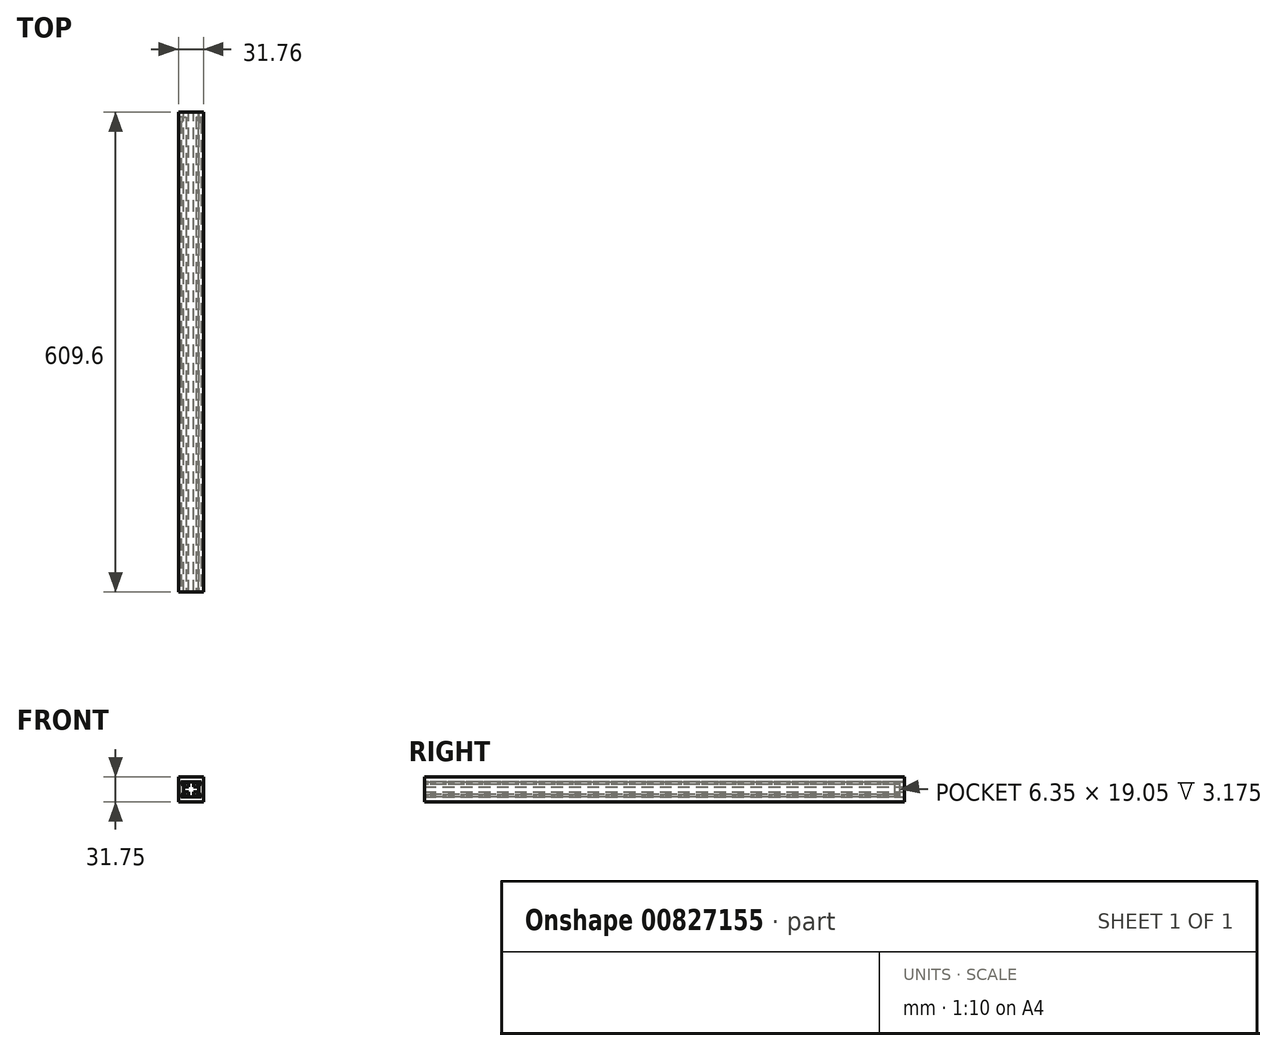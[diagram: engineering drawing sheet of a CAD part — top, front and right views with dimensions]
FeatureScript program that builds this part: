
annotation { "Feature Type Name" : "Feature", "Feature Type Description" : "" }
export const myFeature = defineFeature(function(context is Context, id is Id, definition is map)
    precondition{}
    {
        {
            var Q0;
            Q0=qCreatedBy(makeId("Top.planeOp"),FACE);
            var sketch = newSketch(context, id + "F0", { "sketchPlane" : qUnion([Q0])});
            skLineSegment(sketch, "E0", {"start": v(0, 0) * mm, "end": v(3.17, 0) * mm});
            skLineSegment(sketch, "E1", {"start": v(3.17, 0) * mm, "end": v(-3.17, 0) * mm});
            skLineSegment(sketch, "E2.bottom", {"start": v(3.17, 0) * mm, "end": v(9.53, 0) * mm});
            skLineSegment(sketch, "E2.top", {"start": v(3.18, 609.6) * mm, "end": v(9.53, 609.6) * mm});
            skLineSegment(sketch, "E2.left", {"start": v(3.18, 0) * mm, "end": v(3.18, 609.6) * mm});
            skLineSegment(sketch, "E2.right", {"start": v(9.53, 0) * mm, "end": v(9.53, 609.6) * mm});
            skLineSegment(sketch, "E3.bottom", {"start": v(-3.17, 0) * mm, "end": v(-9.53, 0) * mm});
            skLineSegment(sketch, "E3.top", {"start": v(-3.18, 609.6) * mm, "end": v(-9.53, 609.6) * mm});
            skLineSegment(sketch, "E3.left", {"start": v(-3.17, 0) * mm, "end": v(-3.18, 609.6) * mm});
            skLineSegment(sketch, "E3.right", {"start": v(-9.53, 0) * mm, "end": v(-9.53, 609.6) * mm});
            skPoint(sketch, "E4", {"position": v(0, 0) * mm});
            skSolve(sketch);
        }
        {
            var Q0;
            Q0=makeQuery(id+"F0.imprint","IMPRINT",FACE,{"disambiguationData":[TD([[makeQuery(id+"F0.imprint","IMPRINT",EDGE,{"derivedFrom":sQuery(id+"F0.wireOp",EDGE,"E3.bottom")}),-1.0]])]});
            var Q1;
            Q1=makeQuery(id+"F0.imprint","IMPRINT",FACE,{"disambiguationData":[TD([[makeQuery(id+"F0.imprint","IMPRINT",EDGE,{"derivedFrom":sQuery(id+"F0.wireOp",EDGE,"E2.bottom")}),1.0]])]});
            extrude(context, id + "F1", {"entities" : qUnion([Q0, Q1]), "depth" : 6.35 * mm, "offsetDistance" : 25.4 * mm});
        }
        {
            var Q0;
            Q0=qSketchRegion(id+"F0",true);
            extrude(context, id + "F2", {"entities" : qUnion([Q0]), "oppositeDirection" : true, "depth" : 12.7 * mm, "offsetDistance" : 25.4 * mm});
        }
        {
            var Q0;
            Q0=qSketchRegion(id+"F0",true);
            extrude(context, id + "F3", {"entities" : qUnion([Q0]), "operationType" : NewBodyOperationType.REMOVE, "oppositeDirection" : true, "depth" : 6.35 * mm, "offsetDistance" : 25.4 * mm});
        }
        {
            var Q0;
            Q0=qCreatedBy(makeId("Front.planeOp"),FACE);
            var sketch = newSketch(context, id + "F4", { "sketchPlane" : qUnion([Q0])});
            skPoint(sketch, "E5", {"position": v(-9.53, 6.35) * mm});
            skPoint(sketch, "E6", {"position": v(9.53, 6.35) * mm});
            skPoint(sketch, "E7", {"position": v(9.53, -12.7) * mm});
            skPoint(sketch, "E8", {"position": v(-9.53, -12.7) * mm});
            skLineSegment(sketch, "E9", {"start": v(-9.53, 6.35) * mm, "end": v(9.53, 6.35) * mm});
            skLineSegment(sketch, "E10", {"start": v(-9.53, -12.7) * mm, "end": v(9.53, -12.7) * mm});
            skLineSegment(sketch, "E11", {"start": v(9.53, 6.35) * mm, "end": v(9.53, -12.7) * mm});
            skLineSegment(sketch, "E12", {"start": v(-9.53, 6.35) * mm, "end": v(-9.53, -12.7) * mm});
            skLineSegment(sketch, "E13.left", {"start": v(-15.88, 12.7) * mm, "end": v(-15.88, -19.05) * mm});
            skLineSegment(sketch, "E14", {"start": v(-15.88, 12.7) * mm, "end": v(15.88, 12.7) * mm});
            skLineSegment(sketch, "E15", {"start": v(-15.88, -19.05) * mm, "end": v(15.88, -19.05) * mm});
            skLineSegment(sketch, "E16", {"start": v(15.88, -19.05) * mm, "end": v(15.88, 12.7) * mm});
            skSolve(sketch);
        }
        {
            var Q0;
            Q0=makeQuery(id+"F4.imprint","IMPRINT",FACE,{"disambiguationData":[TD([[makeQuery(id+"F4.imprint","IMPRINT",EDGE,{"derivedFrom":sQuery(id+"F4.wireOp",EDGE,"E9")}),1.0]])]});
            extrude(context, id + "F5", {"entities" : qUnion([Q0]), "oppositeDirection" : true, "depth" : 609.6 * mm, "offsetDistance" : 25.4 * mm});
        }
        {
            var Q0;
            Q0=makeQuery(id+"F5.opExtrude","CAP_FACE",FACE,{"disambiguationData":[OSD([sQuery(id+"F4.wireOp",EDGE,"E9"),sQuery(id+"F4.wireOp",EDGE,"E10"),sQuery(id+"F4.wireOp",EDGE,"E11"),sQuery(id+"F4.wireOp",EDGE,"E12"),sQuery(id+"F4.wireOp",EDGE,"E13.left"),sQuery(id+"F4.wireOp",EDGE,"E14"),sQuery(id+"F4.wireOp",EDGE,"E15"),sQuery(id+"F4.wireOp",EDGE,"E16")])],"isStart":true});
            var sketch = newSketch(context, id + "F6", { "sketchPlane" : qUnion([Q0])});
            skPoint(sketch, "E17", {"position": v(6.35, -9.53) * mm});
            skPoint(sketch, "E18", {"position": v(12.7, -12.7) * mm});
            skLineSegment(sketch, "E19.bottom", {"start": v(6.35, -9.53) * mm, "end": v(12.7, -9.53) * mm});
            skLineSegment(sketch, "E19.top", {"start": v(6.35, -12.7) * mm, "end": v(12.7, -12.7) * mm});
            skLineSegment(sketch, "E19.left", {"start": v(6.35, -9.53) * mm, "end": v(6.35, -12.7) * mm});
            skLineSegment(sketch, "E19.right", {"start": v(12.7, -9.53) * mm, "end": v(12.7, -12.7) * mm});
            skPoint(sketch, "E20", {"position": v(-6.35, 3.18) * mm});
            skPoint(sketch, "E21", {"position": v(6.35, 3.17) * mm});
            skPoint(sketch, "E22", {"position": v(-6.35, -9.53) * mm});
            skLineSegment(sketch, "E23.bottom", {"start": v(6.35, 3.17) * mm, "end": v(12.7, 3.17) * mm});
            skLineSegment(sketch, "E23.top", {"start": v(6.35, 6.35) * mm, "end": v(12.7, 6.35) * mm});
            skLineSegment(sketch, "E23.left", {"start": v(6.35, 3.17) * mm, "end": v(6.35, 6.35) * mm});
            skLineSegment(sketch, "E23.right", {"start": v(12.7, 3.17) * mm, "end": v(12.7, 6.35) * mm});
            skLineSegment(sketch, "E24.bottom", {"start": v(-12.7, -9.53) * mm, "end": v(-6.35, -9.53) * mm});
            skLineSegment(sketch, "E24.top", {"start": v(-12.7, -12.7) * mm, "end": v(-6.35, -12.7) * mm});
            skLineSegment(sketch, "E24.left", {"start": v(-12.7, -9.53) * mm, "end": v(-12.7, -12.7) * mm});
            skLineSegment(sketch, "E24.right", {"start": v(-6.35, -9.53) * mm, "end": v(-6.35, -12.7) * mm});
            skLineSegment(sketch, "E25.bottom", {"start": v(-6.35, 3.18) * mm, "end": v(-12.7, 3.18) * mm});
            skLineSegment(sketch, "E25.top", {"start": v(-6.35, 6.35) * mm, "end": v(-12.7, 6.35) * mm});
            skLineSegment(sketch, "E25.left", {"start": v(-6.35, 3.18) * mm, "end": v(-6.35, 6.35) * mm});
            skLineSegment(sketch, "E25.right", {"start": v(-12.7, 3.17) * mm, "end": v(-12.7, 6.35) * mm});
            skSolve(sketch);
        }
        {
            var Q0;
            {var subQ0=sQuery(id+"F6.wireOp",EDGE,"E25.right");Q0=makeQuery(id+"F6.imprint","IMPRINT",FACE,{"disambiguationData":[TD([[makeQuery(id+"F6.imprint","IMPRINT",EDGE,{"derivedFrom":subQ0}),-1.0]])]});}
            var Q1;
            {var subQ0=sQuery(id+"F6.wireOp",EDGE,"E25.left");Q1=makeQuery(id+"F6.imprint","IMPRINT",FACE,{"disambiguationData":[TD([[makeQuery(id+"F6.imprint","IMPRINT",EDGE,{"derivedFrom":subQ0}),1.0]])]});}
            var Q2;
            {var subQ0=sQuery(id+"F6.wireOp",EDGE,"E23.left");Q2=makeQuery(id+"F6.imprint","IMPRINT",FACE,{"disambiguationData":[TD([[makeQuery(id+"F6.imprint","IMPRINT",EDGE,{"derivedFrom":subQ0}),-1.0]])]});}
            var Q3;
            {var subQ0=sQuery(id+"F6.wireOp",EDGE,"E23.right");Q3=makeQuery(id+"F6.imprint","IMPRINT",FACE,{"disambiguationData":[TD([[makeQuery(id+"F6.imprint","IMPRINT",EDGE,{"derivedFrom":subQ0}),1.0]])]});}
            var Q4;
            {var subQ0=sQuery(id+"F6.wireOp",EDGE,"E24.left");Q4=makeQuery(id+"F6.imprint","IMPRINT",FACE,{"disambiguationData":[TD([[makeQuery(id+"F6.imprint","IMPRINT",EDGE,{"derivedFrom":subQ0}),1.0]])]});}
            var Q5;
            {var subQ0=sQuery(id+"F6.wireOp",EDGE,"E24.right");Q5=makeQuery(id+"F6.imprint","IMPRINT",FACE,{"disambiguationData":[TD([[makeQuery(id+"F6.imprint","IMPRINT",EDGE,{"derivedFrom":subQ0}),-1.0]])]});}
            var Q6;
            {var subQ0=sQuery(id+"F6.wireOp",EDGE,"E19.left");Q6=makeQuery(id+"F6.imprint","IMPRINT",FACE,{"disambiguationData":[TD([[makeQuery(id+"F6.imprint","IMPRINT",EDGE,{"derivedFrom":subQ0}),1.0]])]});}
            var Q7;
            {var subQ0=sQuery(id+"F6.wireOp",EDGE,"E19.right");Q7=makeQuery(id+"F6.imprint","IMPRINT",FACE,{"disambiguationData":[TD([[makeQuery(id+"F6.imprint","IMPRINT",EDGE,{"derivedFrom":subQ0}),-1.0]])]});}
            extrude(context, id + "F7", {"entities" : qUnion([Q0, Q1, Q2, Q3, Q4, Q5, Q6, Q7]), "operationType" : NewBodyOperationType.REMOVE, "oppositeDirection" : true, "depth" : 603.25 * mm, "offsetDistance" : 25.4 * mm});
        }
        {
            var Q0;
            Q0=makeQuery(id+"F5.opExtrude","CAP_FACE",FACE,{"disambiguationData":[OSD([sQuery(id+"F4.wireOp",EDGE,"E9"),sQuery(id+"F4.wireOp",EDGE,"E10"),sQuery(id+"F4.wireOp",EDGE,"E11"),sQuery(id+"F4.wireOp",EDGE,"E12"),sQuery(id+"F4.wireOp",EDGE,"E13.left"),sQuery(id+"F4.wireOp",EDGE,"E14"),sQuery(id+"F4.wireOp",EDGE,"E15"),sQuery(id+"F4.wireOp",EDGE,"E16")])],"isStart":false});
            var sketch = newSketch(context, id + "F8", { "sketchPlane" : qUnion([Q0])});
            skLineSegment(sketch, "E26.right", {"start": v(-13.97, 6.35) * mm, "end": v(-13.97, -12.7) * mm});
            skLineSegment(sketch, "E27.bottom", {"start": v(-13.97, 6.35) * mm, "end": v(-10.8, 6.35) * mm});
            skLineSegment(sketch, "E27.top", {"start": v(-13.97, -12.7) * mm, "end": v(-10.8, -12.7) * mm});
            skLineSegment(sketch, "E27.right", {"start": v(-10.8, 6.35) * mm, "end": v(-10.8, -12.7) * mm});
            skLineSegment(sketch, "E28.bottom", {"start": v(10.8, 6.35) * mm, "end": v(13.97, 6.35) * mm});
            skLineSegment(sketch, "E28.top", {"start": v(10.8, -12.7) * mm, "end": v(13.97, -12.7) * mm});
            skLineSegment(sketch, "E28.left", {"start": v(10.8, 6.35) * mm, "end": v(10.8, -12.7) * mm});
            skLineSegment(sketch, "E28.right", {"start": v(13.97, 6.35) * mm, "end": v(13.97, -12.7) * mm});
            skSolve(sketch);
        }
        {
            var Q0;
            {var subQ1=makeQuery(id+"F7.boolean.opBoolean","COPY",EDGE,{"derivedFrom":makeQuery(id+"F7.opExtrude","CAP_EDGE",EDGE,{"disambiguationData":[OSD([sQuery(id+"F6.wireOp",EDGE,"E23.right")])],"isStart":false})});Q0=makeQuery(id+"F8.imprint","IMPRINT",FACE,{"disambiguationData":[TD([[makeQuery(id+"F8.imprint","IMPRINT",EDGE,{"derivedFrom":subQ1}),-1.0]])]});}
            var Q1;
            {var subQ2=sQuery(id+"F8.wireOp",EDGE,"E26.right");Q1=makeQuery(id+"F8.imprint","IMPRINT",FACE,{"disambiguationData":[TD([[makeQuery(id+"F8.imprint","IMPRINT",EDGE,{"derivedFrom":subQ2}),1.0]])]});}
            var Q2;
            {var subQ1=makeQuery(id+"F7.boolean.opBoolean","COPY",EDGE,{"derivedFrom":makeQuery(id+"F7.opExtrude","CAP_EDGE",EDGE,{"disambiguationData":[OSD([sQuery(id+"F6.wireOp",EDGE,"E19.right")])],"isStart":false})});Q2=makeQuery(id+"F8.imprint","IMPRINT",FACE,{"disambiguationData":[TD([[makeQuery(id+"F8.imprint","IMPRINT",EDGE,{"derivedFrom":subQ1}),1.0]])]});}
            extrude(context, id + "F9", {"entities" : qUnion([Q0, Q1, Q2]), "operationType" : NewBodyOperationType.REMOVE, "oppositeDirection" : true, "depth" : 12.7 * mm, "offsetDistance" : 25.4 * mm});
        }
        {
            var Q0;
            {var subQ2=sQuery(id+"F8.wireOp",EDGE,"E26.right");Q0=makeQuery(id+"F8.imprint","IMPRINT",FACE,{"disambiguationData":[TD([[makeQuery(id+"F8.imprint","IMPRINT",EDGE,{"derivedFrom":subQ2}),1.0]])]});}
            var Q1;
            {var subQ1=makeQuery(id+"F7.boolean.opBoolean","COPY",EDGE,{"derivedFrom":makeQuery(id+"F7.opExtrude","CAP_EDGE",EDGE,{"disambiguationData":[OSD([sQuery(id+"F6.wireOp",EDGE,"E23.right")])],"isStart":false})});Q1=makeQuery(id+"F8.imprint","IMPRINT",FACE,{"disambiguationData":[TD([[makeQuery(id+"F8.imprint","IMPRINT",EDGE,{"derivedFrom":subQ1}),-1.0]])]});}
            var Q2;
            {var subQ1=makeQuery(id+"F7.boolean.opBoolean","COPY",EDGE,{"derivedFrom":makeQuery(id+"F7.opExtrude","CAP_EDGE",EDGE,{"disambiguationData":[OSD([sQuery(id+"F6.wireOp",EDGE,"E19.right")])],"isStart":false})});Q2=makeQuery(id+"F8.imprint","IMPRINT",FACE,{"disambiguationData":[TD([[makeQuery(id+"F8.imprint","IMPRINT",EDGE,{"derivedFrom":subQ1}),1.0]])]});}
            extrude(context, id + "F10", {"entities" : qUnion([Q0, Q1, Q2]), "operationType" : NewBodyOperationType.ADD, "oppositeDirection" : true, "depth" : 6.35 * mm, "offsetDistance" : 25.4 * mm});
        }
        {
            var Q0;
            Q0=makeQuery(id+"F8.imprint","IMPRINT",FACE,{"disambiguationData":[TD([[makeQuery(id+"F8.imprint","IMPRINT",EDGE,{"derivedFrom":sQuery(id+"F8.wireOp",EDGE,"E28.bottom")}),-1.0]])]});
            extrude(context, id + "F11", {"entities" : qUnion([Q0]), "operationType" : NewBodyOperationType.REMOVE, "oppositeDirection" : true, "depth" : 12.7 * mm, "offsetDistance" : 25.4 * mm});
        }
        {
            var Q0;
            Q0=makeQuery(id+"F8.imprint","IMPRINT",FACE,{"disambiguationData":[TD([[makeQuery(id+"F8.imprint","IMPRINT",EDGE,{"derivedFrom":sQuery(id+"F8.wireOp",EDGE,"E28.bottom")}),-1.0]])]});
            extrude(context, id + "F12", {"entities" : qUnion([Q0]), "operationType" : NewBodyOperationType.ADD, "oppositeDirection" : true, "depth" : 6.35 * mm, "offsetDistance" : 25.4 * mm});
        }
    });
